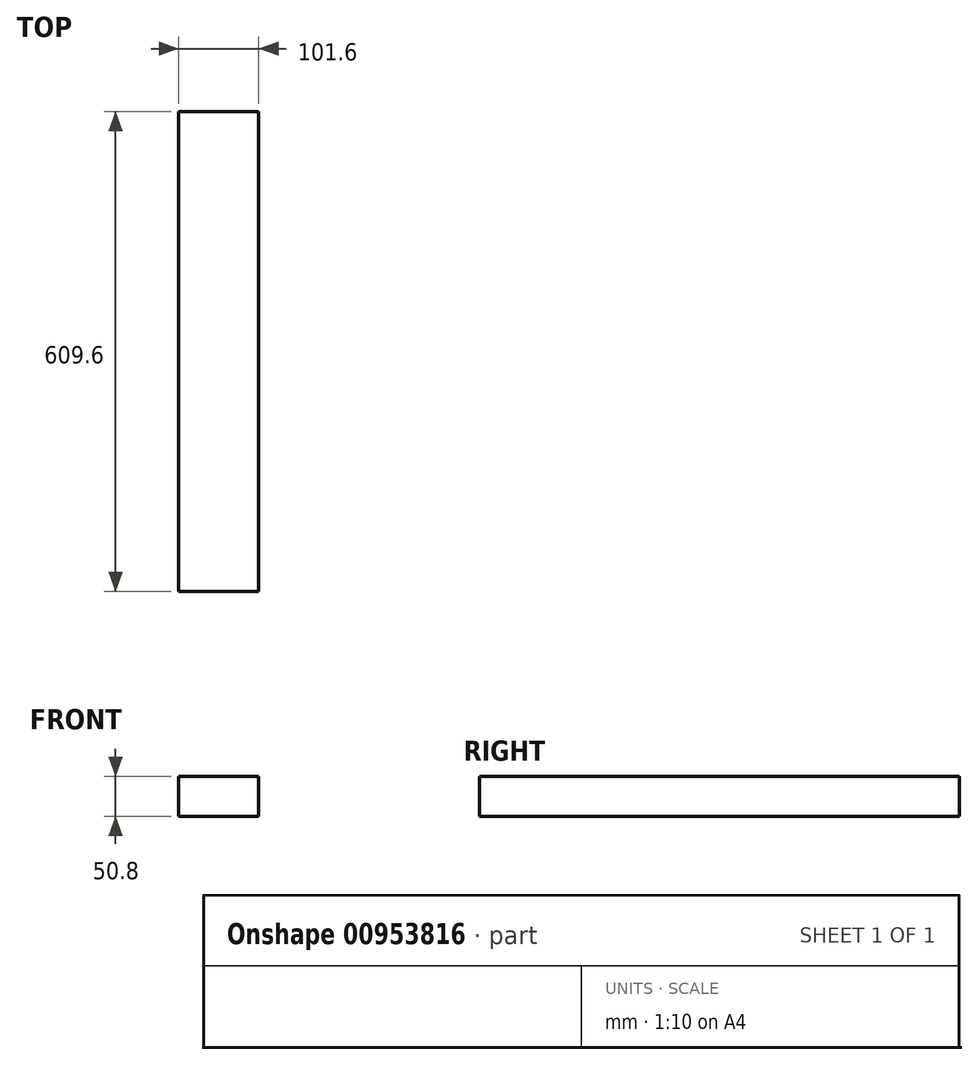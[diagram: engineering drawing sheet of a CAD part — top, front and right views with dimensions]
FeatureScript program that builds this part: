
annotation { "Feature Type Name" : "Feature", "Feature Type Description" : "" }
export const myFeature = defineFeature(function(context is Context, id is Id, definition is map)
    precondition{}
    {
        {
            var Q0;
            Q0=qCreatedBy(makeId("Front.planeOp"),FACE);
            var sketch = newSketch(context, id + "F0", { "sketchPlane" : qUnion([Q0])});
            skLineSegment(sketch, "E0.bottom", {"start": v(-50.8, -25.4) * mm, "end": v(50.8, -25.4) * mm});
            skLineSegment(sketch, "E0.top", {"start": v(-50.8, 25.4) * mm, "end": v(50.8, 25.4) * mm});
            skLineSegment(sketch, "E0.left", {"start": v(-50.8, -25.4) * mm, "end": v(-50.8, 25.4) * mm});
            skLineSegment(sketch, "E0.right", {"start": v(50.8, -25.4) * mm, "end": v(50.8, 25.4) * mm});
            skPoint(sketch, "E0.middle", {"position": v(0, 0) * mm});
            skSolve(sketch);
        }
        {
            var Q0;
            Q0 = qSketchRegion(id + "F0", true);
            extrude(context, id + "F1", {"entities" : qUnion([Q0]), "depth" : 609.6 * mm, "offsetDistance" : 25.4 * mm});
        }
    });
